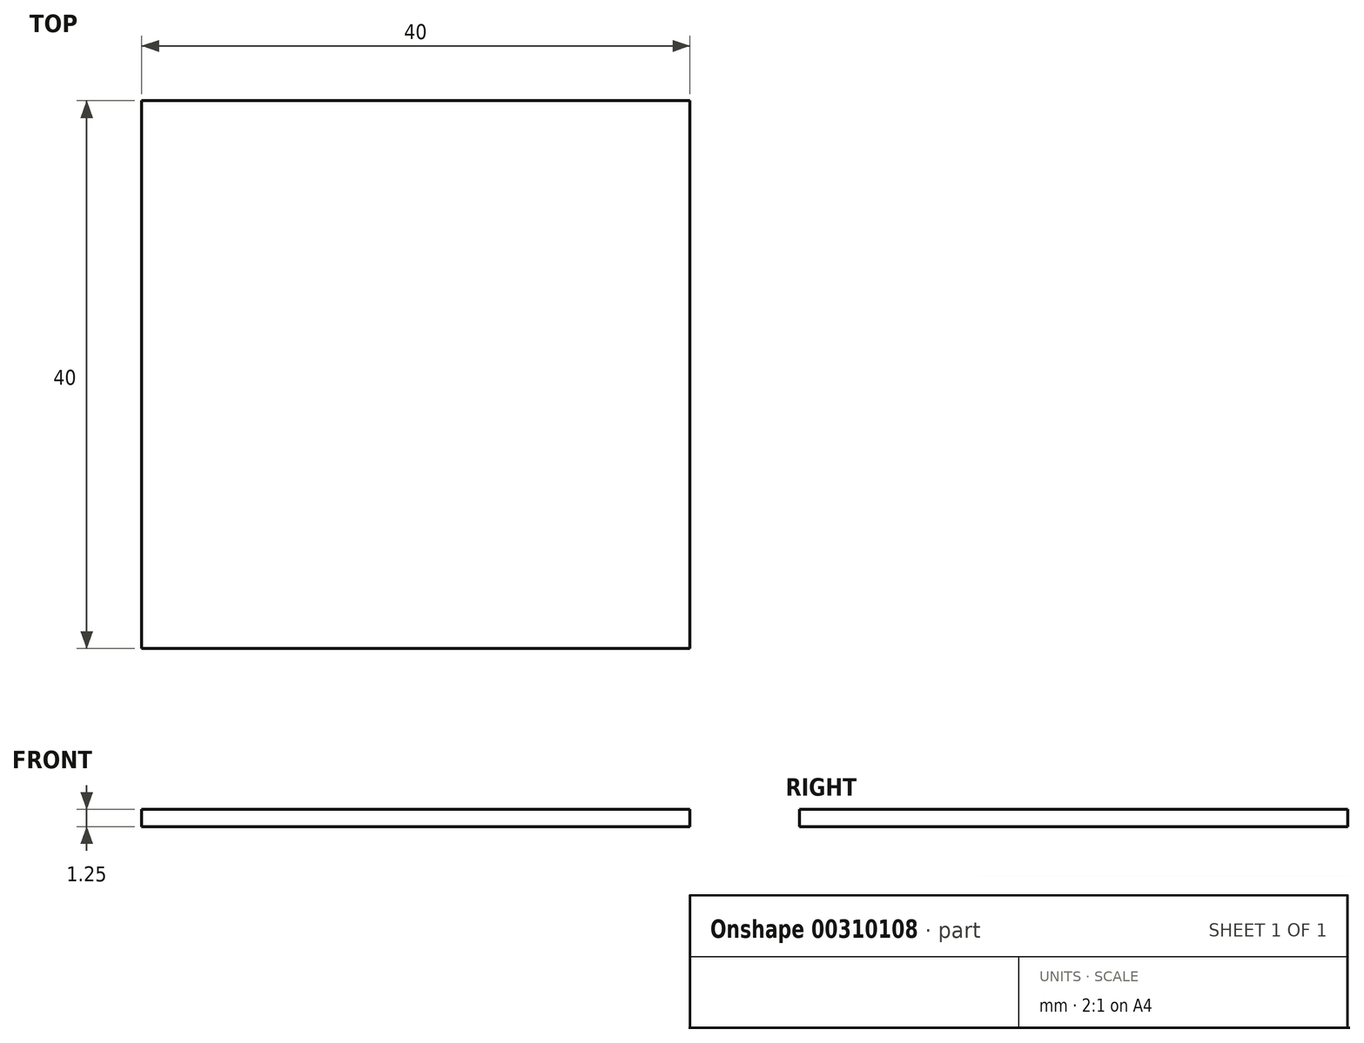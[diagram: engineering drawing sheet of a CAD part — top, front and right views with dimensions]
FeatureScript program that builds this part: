
annotation { "Feature Type Name" : "Feature", "Feature Type Description" : "" }
export const myFeature = defineFeature(function(context is Context, id is Id, definition is map)
    precondition{}
    {
        {
            var Q0;
            Q0=qCreatedBy(makeId("Top.planeOp"),FACE);
            var sketch = newSketch(context, id + "F0", { "sketchPlane" : qUnion([Q0])});
            skLineSegment(sketch, "E0", {"start": v(0, 0) * mm, "end": v(0, -40) * mm});
            skLineSegment(sketch, "E1", {"start": v(0, -40) * mm, "end": v(40, -40) * mm});
            skLineSegment(sketch, "E2", {"start": v(40, -40) * mm, "end": v(40, 0) * mm});
            skLineSegment(sketch, "E3", {"start": v(0, 0) * mm, "end": v(40, 0) * mm});
            skSolve(sketch);
        }
        {
            var Q0;
            Q0 = qSketchRegion(id + "F0", true);
            extrude(context, id + "F1", {"entities" : qUnion([Q0]), "depth" : 1.25 * mm});
        }
    });
